# Revit family: HARVEY_2x50W_2xE27
name_source: partatom
category: Lighting Fixtures
units: mm (PartAtom-declared; Revit-internal decimal feet)

## family parameters
Always vertical = Yes
Cut with Voids When Loaded = No
Host = Wall
Light Source = Yes
OmniClass Number = 23.80.70.00
OmniClass Title = Lighting
Part Type = Normal
Room Calculation Point = No
Round Connector Dimension = Use Diameter
Shared = No

## types (1)
- HARVEY_2x50W_2xE27
    Alimentation Driver = AC 220-240V / 50Hz
    Angle du faisceau = 15°/30°/45°
    Color Filter = 16777215
    Default Elevation = 0 mm  [stored 0 ft]
    Diffuseur = Verre trempé
    Dimensions = 157 x 224 mm
    Dimming Lamp Color Temperature Shift = <None>
    Emit Shape Visible in Rendering = No
    Emit from Rectangle Length = 1219 mm
    Emit from Rectangle Width = 610 mm
    Fintion = Gris anthracite
    Matériau = Corps en aluminium moulé sous pression
    Photometric Web File = generic
    Puissance nominale = Max 2x50W
    Tilt Angle = 90.00°
    Type = Applique murale
    Type de douille = 2xE27
    Type de lampe = LED

note: [stored X ft] marks values corroborated as IEEE doubles in the binary element streams (Revit-internal decimal feet)

## geometry (parser evidence)
native form markers: Sweep x3
no freeform markers — native parametric forms only
